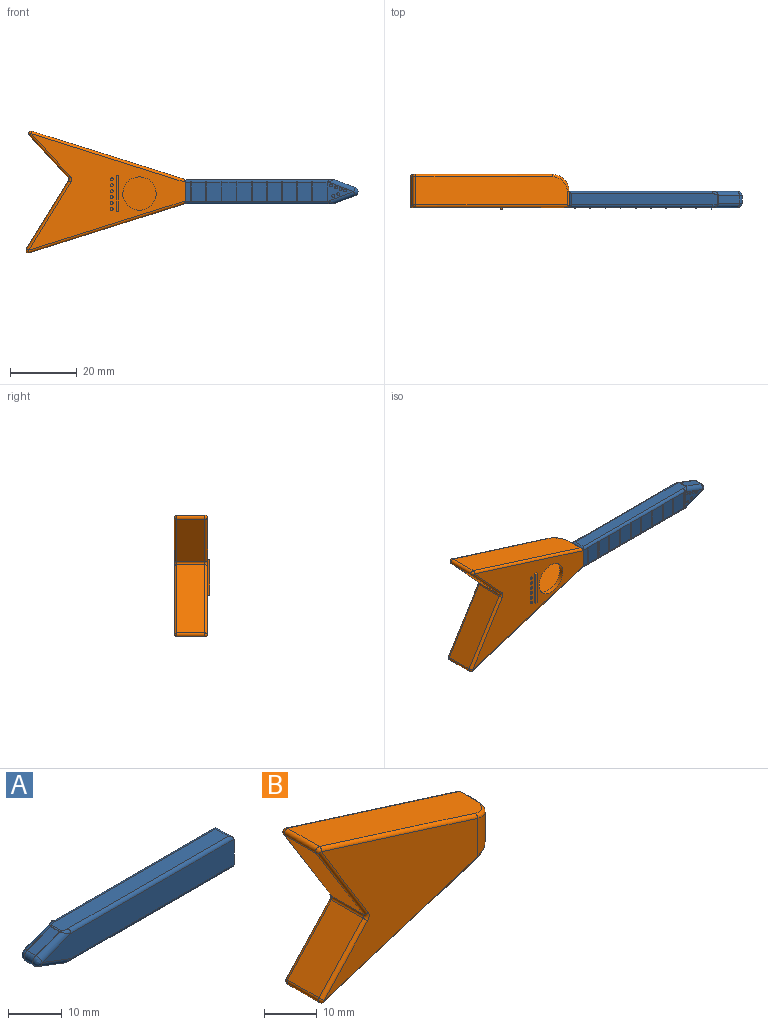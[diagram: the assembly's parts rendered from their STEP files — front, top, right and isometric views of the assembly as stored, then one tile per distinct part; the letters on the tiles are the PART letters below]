
ASSEMBLY  parts=2 mates=1
PART A: 94 faces, bbox 51.6x5.5x8.1 mm
  f0: plane 5.62x0.54mm, normal (1,0,0), area 3mm2, adj f1,f3,f50,f52,f79
  f1: plane 0.54x0.26mm, normal (0,0,1), area 0.1mm2, adj f0,f2,f52,f79
  f2: plane 5.62x0.54mm, normal (-1,0,0), area 3mm2, adj f1,f3,f50,f52,f79
  f3: plane 0.53x0.25mm, normal (0,0,-1), area 0.1mm2, adj f0,f2,f50,f79
  f4: plane 5.62x0.24mm, normal (1,0,0), area 1.3mm2, adj f5,f7,f8,f50,f52
  f5: plane 0.26x0.24mm, normal (0,0,1), area 0.1mm2, adj f4,f6,f8,f52
  f6: plane 5.62x0.24mm, normal (-1,0,0), area 1.3mm2, adj f5,f7,f8,f50,f52
  f7: plane 0.25x0.23mm, normal (0,0,-1), area 0.1mm2, adj f4,f6,f8,f50
  f8: plane 5.61x0.25mm, normal (0,1,0), area 1.4mm2, adj f4,f5,f6,f7
  f9: plane 5.62x0.24mm, normal (1,0,0), area 1.3mm2, adj f10,f12,f13,f50,f52
  f10: plane 0.26x0.24mm, normal (0,0,1), area 0.1mm2, adj f9,f11,f13,f52
  f11: plane 5.62x0.24mm, normal (-1,0,0), area 1.3mm2, adj f10,f12,f13,f50,f52
  f12: plane 0.25x0.23mm, normal (0,0,-1), area 0.1mm2, adj f9,f11,f13,f50
  f13: plane 5.61x0.25mm, normal (0,1,0), area 1.4mm2, adj f9,f10,f11,f12
  f14: plane 5.62x0.24mm, normal (1,0,0), area 1.3mm2, adj f15,f17,f18,f50,f52
  f15: plane 0.26x0.24mm, normal (0,0,1), area 0.1mm2, adj f14,f16,f18,f52
  f16: plane 5.62x0.24mm, normal (-1,0,0), area 1.3mm2, adj f15,f17,f18,f50,f52
  f17: plane 0.25x0.23mm, normal (0,0,-1), area 0.1mm2, adj f14,f16,f18,f50
  f18: plane 5.61x0.25mm, normal (0,1,0), area 1.4mm2, adj f14,f15,f16,f17
  f19: plane 5.62x0.24mm, normal (1,0,0), area 1.3mm2, adj f20,f22,f23,f50,f52
  f20: plane 0.26x0.24mm, normal (0,0,1), area 0.1mm2, adj f19,f21,f23,f52
  f21: plane 5.62x0.24mm, normal (-1,0,0), area 1.3mm2, adj f20,f22,f23,f50,f52
  f22: plane 0.25x0.23mm, normal (0,0,-1), area 0.1mm2, adj f19,f21,f23,f50
  f23: plane 5.61x0.25mm, normal (0,1,0), area 1.4mm2, adj f19,f20,f21,f22
  f24: plane 5.62x0.24mm, normal (1,0,0), area 1.3mm2, adj f25,f27,f28,f50,f52
  f25: plane 0.26x0.24mm, normal (0,0,1), area 0.1mm2, adj f24,f26,f28,f52
  f26: plane 5.62x0.24mm, normal (-1,0,0), area 1.3mm2, adj f25,f27,f28,f50,f52
  f27: plane 0.25x0.23mm, normal (0,0,-1), area 0.1mm2, adj f24,f26,f28,f50
  f28: plane 5.61x0.25mm, normal (0,1,0), area 1.4mm2, adj f24,f25,f26,f27
  f29: plane 5.62x0.24mm, normal (1,0,0), area 1.3mm2, adj f30,f32,f33,f50,f52
  f30: plane 0.26x0.24mm, normal (0,0,1), area 0.1mm2, adj f29,f31,f33,f52
  f31: plane 5.62x0.24mm, normal (-1,0,0), area 1.3mm2, adj f30,f32,f33,f50,f52
  f32: plane 0.25x0.23mm, normal (0,0,-1), area 0.1mm2, adj f29,f31,f33,f50
  f33: plane 5.61x0.25mm, normal (0,1,0), area 1.4mm2, adj f29,f30,f31,f32
  f34: plane 5.62x0.24mm, normal (1,0,0), area 1.3mm2, adj f35,f37,f38,f50,f52
  f35: plane 0.26x0.24mm, normal (0,0,1), area 0.1mm2, adj f34,f36,f38,f52
  f36: plane 5.62x0.24mm, normal (-1,0,0), area 1.3mm2, adj f35,f37,f38,f50,f52
  f37: plane 0.25x0.23mm, normal (0,0,-1), area 0.1mm2, adj f34,f36,f38,f50
  f38: plane 5.61x0.25mm, normal (0,1,0), area 1.4mm2, adj f34,f35,f36,f37
  f39: plane 5.62x0.24mm, normal (1,0,0), area 1.3mm2, adj f40,f42,f43,f50,f52
  f40: plane 0.26x0.24mm, normal (0,0,1), area 0.1mm2, adj f39,f41,f43,f52
  f41: plane 5.62x0.24mm, normal (-1,0,0), area 1.3mm2, adj f40,f42,f43,f50,f52
  f42: plane 0.25x0.23mm, normal (0,0,-1), area 0.1mm2, adj f39,f41,f43,f50
  f43: plane 5.61x0.25mm, normal (0,1,0), area 1.4mm2, adj f39,f40,f41,f42
  f44: plane 5.69x4.83mm, normal (1,0,0), area 27.5mm2, adj f49,f50,f53,f56
  f45: plane 43.46x3.3mm, normal (0,0,1), area 143.2mm2, adj f51,f52,f53,f57,f60,f65
  f46: plane 6.15x2.34mm, normal (-0.35,0,0.93), area 15mm2, adj f59,f60,f67,f68
  f47: plane 6.15x2.34mm, normal (-0.35,0,-0.93), area 15mm2, adj f62,f67,f69,f72
  f48: plane 43.46x3.3mm, normal (0,0,-1), area 143.2mm2, adj f54,f55,f56,f61,f69,f73
  f49: plane 50.37x5.69mm, normal (0,-1,0), area 265.3mm2, adj f44,f51,f54,f68,f72
  f50: plane 50.37x5.69mm, normal (0,1,0), area 247.5mm2, adj f0,f2,f3,f4,f6,f7,f9,f11
  f51: cylinder r=0.76mm len=42.88mm, axis (1,0,0), area 50.9mm2, adj f45,f49,f53,f65
  f52: cylinder r=0.76mm len=42.88mm, axis (-1,0,0), area 50.8mm2, adj f0,f1,f2,f4,f5,f6,f9,f10
  f53: cylinder r=0.76mm len=4.83mm, axis (0,-1,0), area 4.9mm2, adj f44,f45,f51,f52
  f54: cylinder r=0.76mm len=42.88mm, axis (-1,0,0), area 50.9mm2, adj f48,f49,f56,f73
  f55: cylinder r=0.76mm len=42.88mm, axis (1,0,0), area 50.9mm2, adj f48,f50,f56,f61
  f56: cylinder r=0.76mm len=4.83mm, axis (0,1,0), area 4.9mm2, adj f44,f48,f54,f55
  f57: bspline ~1.97x1.28mm, area 1.3mm2, adj f45,f52,f58,f59
  f58: bspline ~0.53x0.52mm, area 0.1mm2, adj f57,f59,f60
  f59: cylinder r=1.27mm len=7.94mm, axis (-0.93,0,-0.35), area 14.4mm2, adj f46,f50,f57,f58,f63
  f60: cylinder r=1.27mm len=2.65mm, axis (0,1,0), area 1.1mm2, adj f45,f46,f58,f64
  f61: bspline ~1.97x1.28mm, area 1.3mm2, adj f48,f55,f62,f66
  f62: cylinder r=1.27mm len=7.94mm, axis (0.93,0,-0.35), area 14.4mm2, adj f47,f50,f61,f63,f66
  f63: sphere r=1.27mm, area 2.7mm2, adj f59,f62,f67
  f64: bspline ~0.53x0.52mm, area 0.1mm2, adj f60,f65,f68
  f65: bspline ~1.97x1.28mm, area 1.3mm2, adj f45,f51,f64,f68
  f66: bspline ~0.53x0.52mm, area 0.1mm2, adj f61,f62,f69
  f67: cylinder r=1.27mm len=2.37mm, axis (0,-1,0), area 7mm2, adj f46,f47,f63,f70
  f68: cylinder r=1.27mm len=7.94mm, axis (0.93,0,0.35), area 14.4mm2, adj f46,f49,f64,f65,f70
  f69: cylinder r=1.27mm len=2.65mm, axis (0,1,0), area 1.1mm2, adj f47,f48,f66,f71
  f70: sphere r=1.27mm, area 2.7mm2, adj f67,f68,f72
  f71: bspline ~0.53x0.52mm, area 0.1mm2, adj f69,f72,f73
  f72: cylinder r=1.27mm len=7.94mm, axis (-0.93,0,0.35), area 14.4mm2, adj f47,f49,f70,f71,f73
  f73: bspline ~1.97x1.28mm, area 1.3mm2, adj f48,f54,f71,f72
  f74: plane 5.62x0.24mm, normal (1,0,0), area 1.3mm2, adj f50,f52,f75,f77,f78
  f75: plane 0.26x0.24mm, normal (0,0,1), area 0.1mm2, adj f52,f74,f76,f78
  f76: plane 5.62x0.24mm, normal (-1,0,0), area 1.3mm2, adj f50,f52,f75,f77,f78
  f77: plane 0.25x0.23mm, normal (0,0,-1), area 0.1mm2, adj f50,f74,f76,f78
  f78: plane 5.61x0.25mm, normal (0,1,0), area 1.4mm2, adj f74,f75,f76,f77
  f79: plane 5.61x0.25mm, normal (0,1,0), area 1.4mm2, adj f0,f1,f2,f3
  f80: cylinder r=0.44mm len=0.89mm, axis (0,1,0), area 2.1mm2, adj f50,f81
  f81: plane 0.89x0.89mm, normal (0,1,0), area 0.6mm2, adj f80
  f82: cylinder r=0.04mm len=0.74mm, axis (0,1,0), area 0.2mm2, adj f84,f85
  f83: cylinder r=0.44mm len=0.89mm, axis (0,1,0), area 2.1mm2, adj f50,f84
  f84: plane 0.89x0.89mm, normal (0,1,0), area 0.6mm2, adj f82,f83
  f85: plane 0.09x0.09mm, normal (0,1,0), area 0mm2, adj f82
  f86: cylinder r=0.44mm len=0.89mm, axis (0,1,0), area 2.1mm2, adj f50,f87
  f87: plane 0.89x0.89mm, normal (0,1,0), area 0.6mm2, adj f86
  f88: cylinder r=0.44mm len=0.89mm, axis (0,1,0), area 2.1mm2, adj f50,f89
  f89: plane 0.89x0.89mm, normal (0,1,0), area 0.6mm2, adj f88
  f90: cylinder r=0.44mm len=0.89mm, axis (0,1,0), area 2.1mm2, adj f50,f91
  f91: plane 0.89x0.89mm, normal (0,1,0), area 0.6mm2, adj f90
  f92: cylinder r=0.44mm len=0.89mm, axis (0,1,0), area 2.1mm2, adj f50,f93
  f93: plane 0.89x0.89mm, normal (0,1,0), area 0.6mm2, adj f92
PART B: 61 faces, bbox 48.2x11.1x36.8 mm
  f0: plane 46.72x34.81mm, normal (0,1,0), area 625.5mm2, adj f1,f16,f17,f18,f19,f20,f22,f24
  f1: plane 6.07x0.51mm, normal (1,0,0), area 3.1mm2, adj f0,f45,f50,f56,f59,f60
  f2: plane 45.96x14.49mm, normal (0.3,0,0.95), area 399.7mm2, adj f48,f54,f58,f59,f60
  f3: plane 20.32x12.56mm, normal (-0.85,0,-0.53), area 200.3mm2, adj f38,f42,f48,f49
  f4: plane 12.66x11.63mm, normal (-0.74,0,0.68), area 144.1mm2, adj f34,f35,f38,f39
  f5: plane 45.2x14.25mm, normal (0.3,0,-0.95), area 393mm2, adj f35,f41,f45,f46,f50
  f6: plane 41.64x34.81mm, normal (0,-1,0), area 678.6mm2, adj f7,f34,f37,f41,f42,f54
  f7: cylinder r=5.08mm len=8.79mm, axis (0,0,-1), area 52.7mm2, adj f6,f46,f53,f58
  f8: plane 5.32x0.44mm, normal (0,1,0), area 2.3mm2, adj f9,f12,f15,f51,f53,f57
  f9: plane 45.08x14.56mm, normal (-0.3,0,-0.95), area 339.9mm2, adj f8,f10,f13,f14,f15,f57
  f10: plane 20.47x12.65mm, normal (0.85,0,0.53), area 177.3mm2, adj f9,f11,f13,f14
  f11: plane 12.39x11.38mm, normal (0.74,0,-0.68), area 123.9mm2, adj f10,f12,f13,f14
  f12: plane 43.81x14.16mm, normal (-0.3,0,0.95), area 330.1mm2, adj f8,f11,f13,f14,f15,f51
  f13: plane 40.49x32.86mm, normal (0,1,0), area 613.7mm2, adj f9,f10,f11,f12,f15
  f14: plane 44.81x32.86mm, normal (0,-1,0), area 563.3mm2, adj f9,f10,f11,f12,f16,f51,f56,f57
  f15: cylinder r=3.81mm len=7.72mm, axis (0,0,-1), area 39mm2, adj f8,f9,f12,f13
  f16: cylinder r=4.98mm len=9.96mm, axis (0,1,0), area 39.7mm2, adj f0,f14
  f17: plane 10.67x0.64mm, normal (1,0,0), area 6.8mm2, adj f0,f18,f20,f21
  f18: plane 0.76x0.64mm, normal (0,0,1), area 0.5mm2, adj f0,f17,f19,f21
  f19: plane 10.67x0.64mm, normal (-1,0,0), area 6.8mm2, adj f0,f18,f20,f21
  f20: plane 0.76x0.64mm, normal (0,0,-1), area 0.5mm2, adj f0,f17,f19,f21
  f21: plane 10.67x0.76mm, normal (0,1,0), area 8.1mm2, adj f17,f18,f19,f20
  f22: cylinder r=0.44mm len=0.87mm, axis (0,1,0), area 1.2mm2, adj f0,f23
  f23: plane 0.87x0.87mm, normal (0,1,0), area 0.6mm2, adj f22
  f24: cylinder r=0.44mm len=0.87mm, axis (0,1,0), area 1.2mm2, adj f0,f25
  f25: plane 0.87x0.87mm, normal (0,1,0), area 0.6mm2, adj f24
  f26: cylinder r=0.44mm len=0.87mm, axis (0,1,0), area 1.2mm2, adj f0,f27
  f27: plane 0.87x0.87mm, normal (0,1,0), area 0.6mm2, adj f26
  f28: cylinder r=0.44mm len=0.87mm, axis (0,1,0), area 1.2mm2, adj f0,f29
  f29: plane 0.87x0.87mm, normal (0,1,0), area 0.6mm2, adj f28
  f30: cylinder r=0.44mm len=0.87mm, axis (0,1,0), area 1.2mm2, adj f0,f31
  f31: plane 0.87x0.87mm, normal (0,1,0), area 0.6mm2, adj f30
  f32: cylinder r=0.44mm len=0.87mm, axis (0,1,0), area 1.2mm2, adj f0,f33
  f33: plane 0.87x0.87mm, normal (0,1,0), area 0.6mm2, adj f32
  f34: cylinder r=0.76mm len=13.17mm, axis (0.68,0,0.74), area 20.6mm2, adj f4,f6,f36,f37
  f35: cylinder r=0.76mm len=8.38mm, axis (0,-1,0), area 16.7mm2, adj f4,f5,f36,f40
  f36: sphere r=0.76mm, area 1.5mm2, adj f34,f35,f41
  f37: torus R=1.52mm, axis (0,-1,0), area 1.6mm2, adj f6,f34,f38,f42
  f38: cylinder r=0.76mm len=8.38mm, axis (0,-1,0), area 8.3mm2, adj f3,f4,f37,f43
  f39: cylinder r=0.76mm len=13.17mm, axis (-0.68,0,-0.74), area 20.6mm2, adj f0,f4,f40,f43
  f40: sphere r=0.76mm, area 1.5mm2, adj f35,f39,f45
  f41: cylinder r=0.76mm len=41.11mm, axis (-0.95,0,-0.3), area 51.3mm2, adj f5,f6,f36,f46
  f42: cylinder r=0.76mm len=20.72mm, axis (-0.53,0,0.85), area 28.6mm2, adj f3,f6,f37,f47
  f43: torus R=1.52mm, axis (0,-1,0), area 1.6mm2, adj f0,f38,f39,f49
  f44: bspline ~1.86x1.19mm, area 0.4mm2, adj f46,f51,f53
  f45: cylinder r=0.76mm len=46.19mm, axis (0.95,0,0.3), area 57.3mm2, adj f0,f1,f5,f40,f50
  f46: bspline ~5.08x5.08mm, area 7.9mm2, adj f5,f7,f41,f44,f50,f53
  f47: sphere r=0.76mm, area 1.3mm2, adj f42,f48,f54
  f48: cylinder r=0.76mm len=8.38mm, axis (0,1,0), area 15.5mm2, adj f2,f3,f47,f55
  f49: cylinder r=0.76mm len=20.72mm, axis (0.53,0,-0.85), area 28.6mm2, adj f0,f3,f43,f55
  f50: cylinder r=0.76mm len=4.79mm, axis (0,-1,0), area 3.7mm2, adj f1,f5,f45,f46,f51,f56
  f51: cylinder r=0.76mm len=4.19mm, axis (0,1,0), area 4.8mm2, adj f8,f12,f14,f44,f50,f56
  f52: bspline ~1.62x1.19mm, area 0.4mm2, adj f53,f57,f58
  f53: cylinder r=0.76mm len=6.36mm, axis (0,0,-1), area 7.4mm2, adj f7,f8,f44,f46,f52,f58
  f54: cylinder r=0.76mm len=41.87mm, axis (0.95,0,-0.3), area 52.3mm2, adj f2,f6,f47,f58
  f55: sphere r=0.76mm, area 1.3mm2, adj f48,f49,f59
  f56: cylinder r=0.76mm len=6.33mm, axis (0,0,-1), area 6.7mm2, adj f1,f14,f50,f51,f57,f60
  f57: cylinder r=0.76mm len=4.19mm, axis (0,-1,0), area 4.8mm2, adj f8,f9,f14,f52,f56,f60
  f58: bspline ~5.96x5.09mm, area 7.9mm2, adj f2,f7,f52,f53,f54,f60
  f59: cylinder r=0.76mm len=46.95mm, axis (-0.95,0,0.3), area 58.2mm2, adj f0,f1,f2,f55,f60
  f60: cylinder r=0.76mm len=4.79mm, axis (0,1,0), area 3.7mm2, adj f1,f2,f56,f57,f58,f59
PLACE A rot(axis=(0,0,-1),180deg) t=(31.85,9.26,-9.65)mm
PLACE B rot(axis=(1,0,0),180deg) t=(39.69,9.26,34.77)mm
MATE fastened A.f44 <-> B.f1  axis (-1,0,0) through (19.7,9.26,6.7)mm
